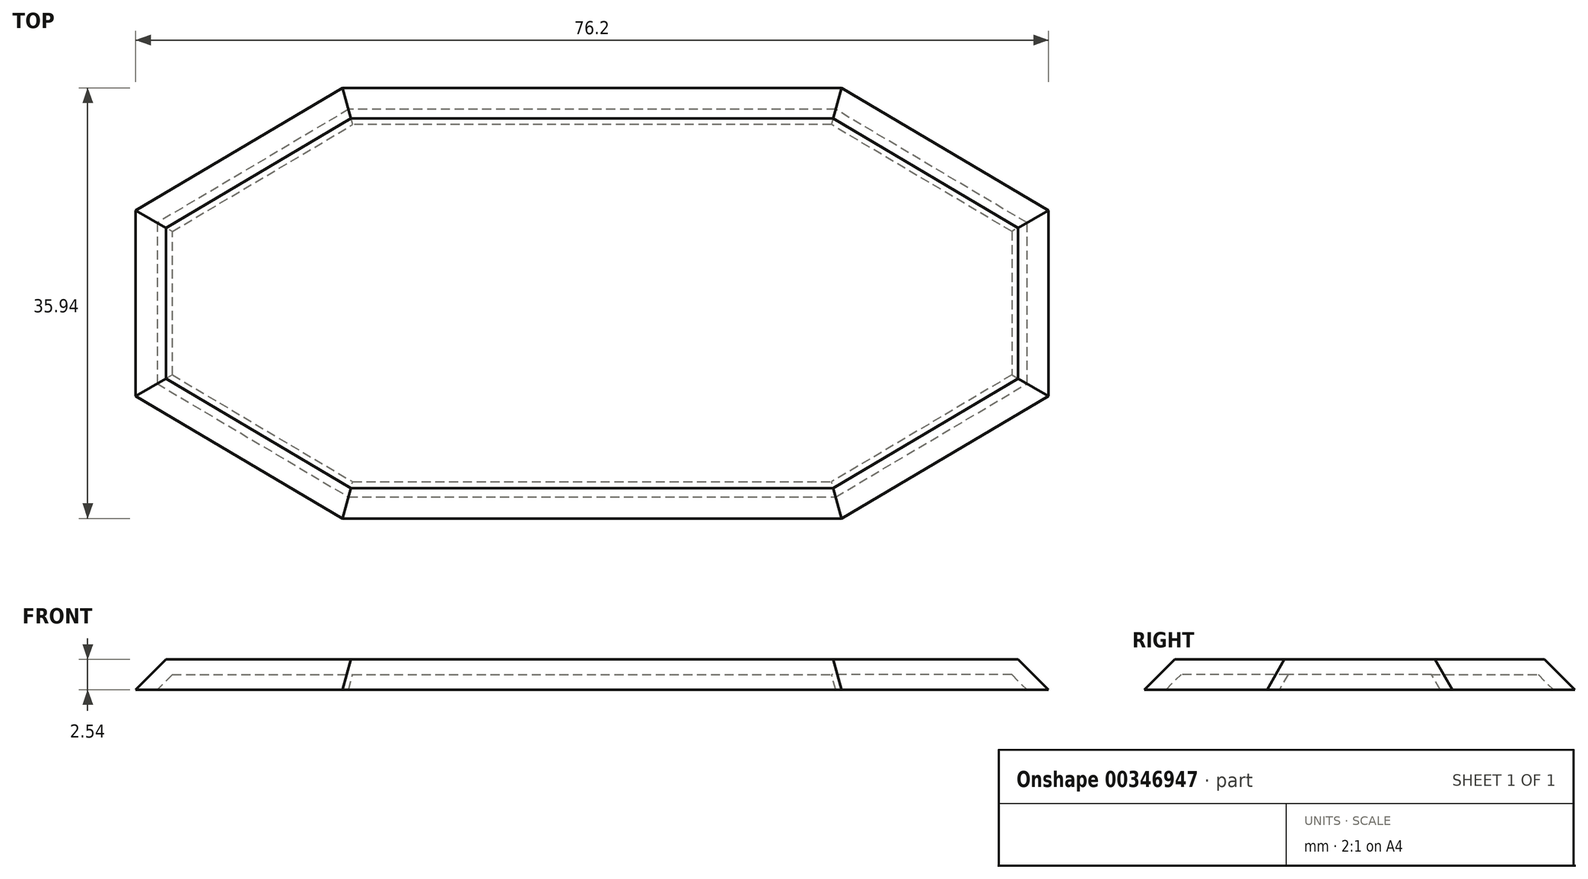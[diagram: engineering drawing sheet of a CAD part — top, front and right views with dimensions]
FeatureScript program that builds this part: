
annotation { "Feature Type Name" : "Feature", "Feature Type Description" : "" }
export const myFeature = defineFeature(function(context is Context, id is Id, definition is map)
    precondition{}
    {
        {
            var Q0;
            Q0=qCreatedBy(makeId("Top.planeOp"),FACE);
            var sketch = newSketch(context, id + "F0", { "sketchPlane" : qUnion([Q0])});
            skLineSegment(sketch, "E0", {"start": v(-38.1, 0) * mm, "end": v(-38.1, -7.74) * mm});
            skLineSegment(sketch, "E1", {"start": v(-38.1, -7.74) * mm, "end": v(-20.82, -17.97) * mm});
            skLineSegment(sketch, "E2", {"start": v(-20.82, -17.97) * mm, "end": v(0, -17.97) * mm});
            skLineSegment(sketch, "E3.MirrorCS", {"start": v(-38.1, 0) * mm, "end": v(-38.1, 7.74) * mm});
            skLineSegment(sketch, "E4.MirrorCS", {"start": v(-38.1, 7.74) * mm, "end": v(-20.82, 17.97) * mm});
            skLineSegment(sketch, "E5.MirrorCS", {"start": v(-20.82, 17.97) * mm, "end": v(0, 17.97) * mm});
            skLineSegment(sketch, "E6.MirrorCS", {"start": v(20.82, 17.97) * mm, "end": v(0, 17.97) * mm});
            skLineSegment(sketch, "E7.MirrorCS", {"start": v(38.1, 7.74) * mm, "end": v(20.82, 17.97) * mm});
            skLineSegment(sketch, "E8.MirrorCS", {"start": v(38.1, 0) * mm, "end": v(38.1, 7.74) * mm});
            skLineSegment(sketch, "E9.MirrorCS", {"start": v(38.1, 0) * mm, "end": v(38.1, -7.74) * mm});
            skLineSegment(sketch, "E10.MirrorCS", {"start": v(38.1, -7.74) * mm, "end": v(20.82, -17.97) * mm});
            skLineSegment(sketch, "E11.MirrorCS", {"start": v(20.82, -17.97) * mm, "end": v(0, -17.97) * mm});
            skSolve(sketch);
        }
        {
            var Q0;
            Q0=makeQuery(id+"F0.imprint","IMPRINT",FACE,{"disambiguationData":[TD([[makeQuery(id+"F0.imprint","IMPRINT",EDGE,{"derivedFrom":sQuery(id+"F0.wireOp",EDGE,"E0")}),1.0]])]});
            extrude(context, id + "F1", {"entities" : qUnion([Q0]), "depth" : 2.54 * mm});
        }
        {
            var Q0;
            Q0=makeQuery(id+"F1.opExtrude","CAP_FACE",FACE,{"disambiguationData":[OSD([sQuery(id+"F0.wireOp",EDGE,"E0"),sQuery(id+"F0.wireOp",EDGE,"E1"),sQuery(id+"F0.wireOp",EDGE,"E2"),sQuery(id+"F0.wireOp",EDGE,"E3.MirrorCS"),sQuery(id+"F0.wireOp",EDGE,"E4.MirrorCS"),sQuery(id+"F0.wireOp",EDGE,"E5.MirrorCS"),sQuery(id+"F0.wireOp",EDGE,"E6.MirrorCS"),sQuery(id+"F0.wireOp",EDGE,"E7.MirrorCS"),sQuery(id+"F0.wireOp",EDGE,"E8.MirrorCS"),sQuery(id+"F0.wireOp",EDGE,"E9.MirrorCS"),sQuery(id+"F0.wireOp",EDGE,"E10.MirrorCS"),sQuery(id+"F0.wireOp",EDGE,"E11.MirrorCS")])],"isStart":false});
            chamfer(context, id + "F2", {"entities" : qUnion([Q0]), "width" : 2.54 * mm, "tangentPropagation" : true});
        }
        {
            var Q0;
            Q0=makeQuery(id+"F1.opExtrude","CAP_FACE",FACE,{"disambiguationData":[OSD([sQuery(id+"F0.wireOp",EDGE,"E0"),sQuery(id+"F0.wireOp",EDGE,"E1"),sQuery(id+"F0.wireOp",EDGE,"E2"),sQuery(id+"F0.wireOp",EDGE,"E3.MirrorCS"),sQuery(id+"F0.wireOp",EDGE,"E4.MirrorCS"),sQuery(id+"F0.wireOp",EDGE,"E5.MirrorCS"),sQuery(id+"F0.wireOp",EDGE,"E6.MirrorCS"),sQuery(id+"F0.wireOp",EDGE,"E7.MirrorCS"),sQuery(id+"F0.wireOp",EDGE,"E8.MirrorCS"),sQuery(id+"F0.wireOp",EDGE,"E9.MirrorCS"),sQuery(id+"F0.wireOp",EDGE,"E10.MirrorCS"),sQuery(id+"F0.wireOp",EDGE,"E11.MirrorCS")])],"isStart":true});
            shell(context, id + "F3", {"entities" : qUnion([Q0]), "thickness" : 1.27 * mm});
        }
    });
